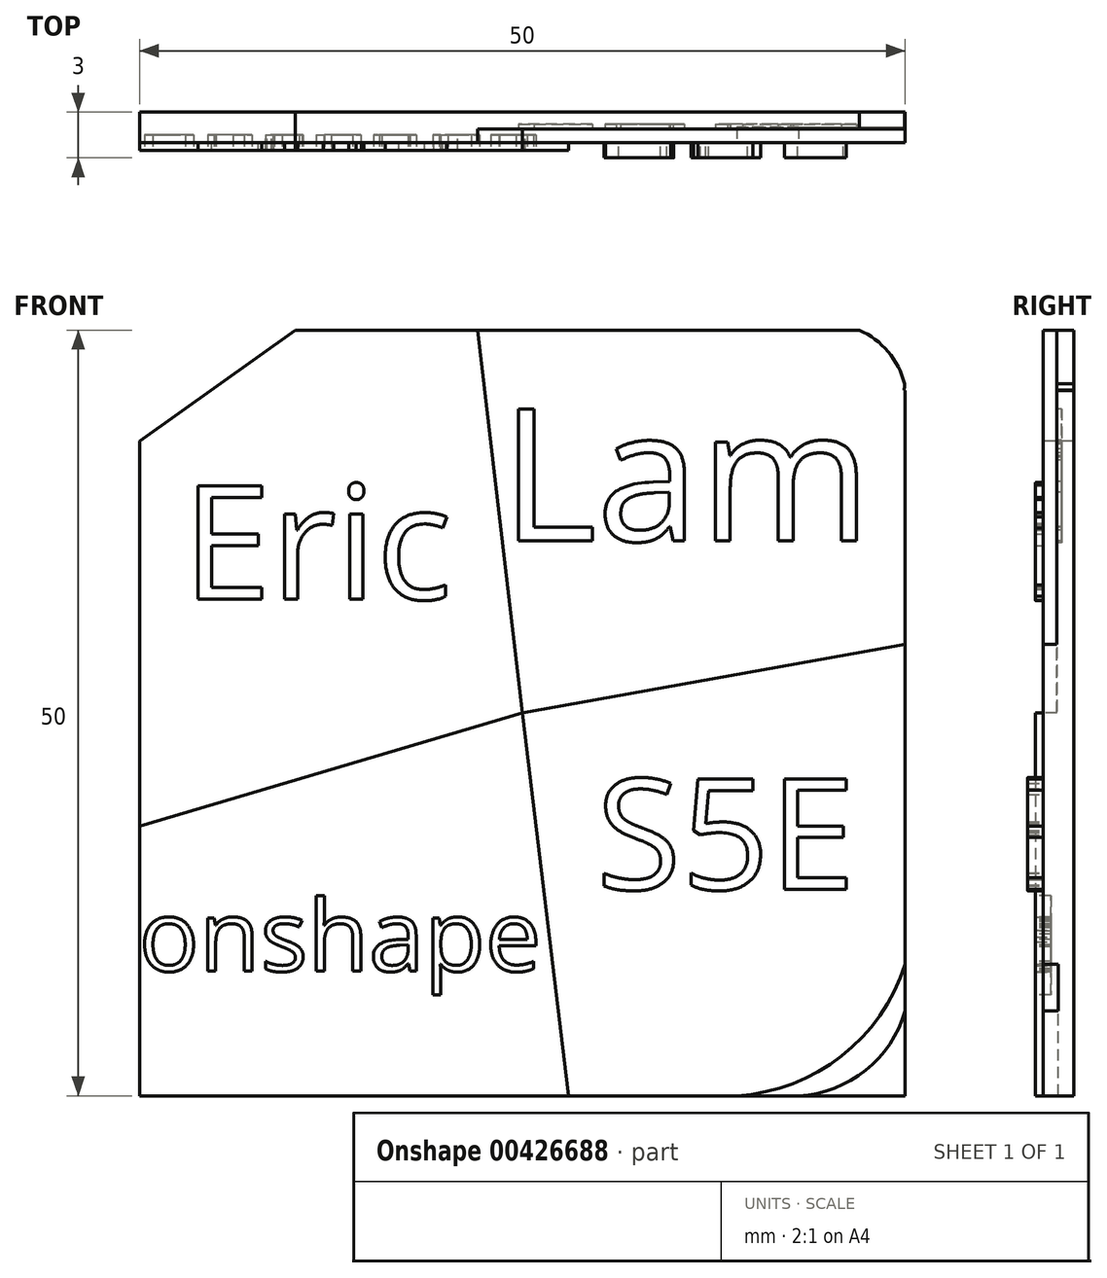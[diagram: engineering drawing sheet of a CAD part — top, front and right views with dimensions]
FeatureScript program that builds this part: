
annotation { "Feature Type Name" : "Feature", "Feature Type Description" : "" }
export const myFeature = defineFeature(function(context is Context, id is Id, definition is map)
    precondition{}
    {
        {
            var Q0;
            Q0=qCreatedBy(makeId("Front.planeOp"),FACE);
            var sketch = newSketch(context, id + "F0", { "sketchPlane" : qUnion([Q0])});
            skLineSegment(sketch, "E0.bottom", {"start": v(25, -25) * mm, "end": v(-25, -25) * mm});
            skLineSegment(sketch, "E0.top", {"start": v(25, 25) * mm, "end": v(-25, 25) * mm});
            skLineSegment(sketch, "E0.left", {"start": v(25, -25) * mm, "end": v(25, 25) * mm});
            skLineSegment(sketch, "E0.right", {"start": v(-25, -25) * mm, "end": v(-25, 25) * mm});
            skPoint(sketch, "E0.middle", {"position": v(0, 0) * mm});
            skLineSegment(sketch, "E1", {"start": v(0, 25) * mm, "end": v(0, 0) * mm});
            skLineSegment(sketch, "E2", {"start": v(0, 0) * mm, "end": v(6.25, -25) * mm});
            skPoint(sketch, "E3.end.orphan", {"position": v(0, -25) * mm});
            skPoint(sketch, "E4.start.orphan", {"position": v(6.25, 0) * mm});
            skPoint(sketch, "E5.end.orphan", {"position": v(12.5, 0) * mm});
            skPoint(sketch, "E6.trimOffspring.end.orphan", {"position": v(25, 0) * mm});
            skLineSegment(sketch, "E7", {"start": v(0, 0) * mm, "end": v(-6.25, -25) * mm});
            skSolve(sketch);
        }
        {
            var Q0;
            Q0 = qSketchRegion(id + "F0", true);
            extrude(context, id + "F1", {"entities" : qUnion([Q0]), "oppositeDirection" : true, "depth" : 2 * mm});
        }
        {
            var Q0;
            Q0=makeQuery(id+"F1.opExtrude","CAP_FACE",FACE,{"disambiguationData":[OSD([sQuery(id+"F0.wireOp",EDGE,"E0.bottom"),sQuery(id+"F0.wireOp",EDGE,"E0.top"),sQuery(id+"F0.wireOp",EDGE,"E0.left"),sQuery(id+"F0.wireOp",EDGE,"E0.right")])],"isStart":true});
            var sketch = newSketch(context, id + "F2", { "sketchPlane" : qUnion([Q0])});
            skLineSegment(sketch, "E8", {"start": v(0, 0) * mm, "end": v(25, 4.5) * mm});
            skPoint(sketch, "E9.orphan", {"position": v(0, 25) * mm});
            skPoint(sketch, "E10.end.orphan", {"position": v(0, -25) * mm});
            skLineSegment(sketch, "E11", {"start": v(0, 0) * mm, "end": v(7.46, -25) * mm});
            skLineSegment(sketch, "E12", {"start": v(-2.93, 25) * mm, "end": v(0, 0) * mm});
            skLineSegment(sketch, "E13", {"start": v(0, 0) * mm, "end": v(-25, -4.25) * mm});
            skSolve(sketch);
        }
        {
            var Q0;
            Q0 = qSketchRegion(id + "F2", true);
            var Q1;
            {var subQ0=sQuery(id+"F2.wireOp",EDGE,"E8");Q1=makeQuery(id+"F2.imprint","IMPRINT",FACE,{"disambiguationData":[TD([[makeQuery(id+"F2.imprint","IMPRINT",EDGE,{"derivedFrom":subQ0}),1.0]])]});}
            extrude(context, id + "F3", {"entities" : qUnion([Q0, Q1]), "operationType" : NewBodyOperationType.REMOVE, "oppositeDirection" : true, "depth" : 0.9 * mm});
        }
        {
            var Q0;
            Q0=makeQuery(id+"F1.opExtrude","CAP_FACE",FACE,{"disambiguationData":[OSD([sQuery(id+"F0.wireOp",EDGE,"E0.bottom"),sQuery(id+"F0.wireOp",EDGE,"E0.top"),sQuery(id+"F0.wireOp",EDGE,"E0.left"),sQuery(id+"F0.wireOp",EDGE,"E0.right")])],"isStart":true});
            var sketch = newSketch(context, id + "F4", { "sketchPlane" : qUnion([Q0])});
            skLineSegment(sketch, "E14", {"start": v(0, 0) * mm, "end": v(-25, -7.38) * mm});
            skLineSegment(sketch, "E15", {"start": v(0, 0) * mm, "end": v(3.03, -25) * mm});
            skSolve(sketch);
        }
        {
            var Q0;
            Q0 = qSketchRegion(id + "F4", true);
            var Q1;
            {var subQ0=sQuery(id+"F4.wireOp",EDGE,"E14");Q1=makeQuery(id+"F4.imprint","IMPRINT",FACE,{"disambiguationData":[TD([[makeQuery(id+"F4.imprint","IMPRINT",EDGE,{"derivedFrom":subQ0}),1.0]])]});}
            extrude(context, id + "F5", {"entities" : qUnion([Q0, Q1]), "operationType" : NewBodyOperationType.ADD, "depth" : 0.5 * mm});
        }
        {
            var Q0;
            {var subQ0=sQuery(id+"F0.wireOp",EDGE,"E0.right");var subQ1=sQuery(id+"F0.wireOp",EDGE,"E0.top");var subQ2=makeQuery(id+"F1.opExtrude","CAP_FACE",FACE,{"disambiguationData":[OSD([sQuery(id+"F0.wireOp",EDGE,"E0.bottom"),subQ1,sQuery(id+"F0.wireOp",EDGE,"E0.left"),subQ0])],"isStart":true});Q0=makeQuery(id+"F5.boolean.opBoolean","SPLIT",FACE,{"disambiguationData":[TD([makeQuery(id+"F1.opExtrude","SWEPT_FACE",FACE,{"disambiguationData":[OSD([subQ1])]})])],"derivedFrom":subQ2});}
            var sketch = newSketch(context, id + "F6", { "sketchPlane" : qUnion([Q0])});
            skText(sketch, "E16", { "text": "Eric\n", "fontName": "OpenSans-Regular.ttf"});
            const initialGuessF6  = {"E16": [-0.02218, 0.00743, 1, 0, 0.00748]};
            skSetInitialGuess(sketch, initialGuessF6);
            skSolve(sketch);
        }
        {
            var Q0;
            Q0 = qSketchRegion(id + "F6", true);
            extrude(context, id + "F7", {"entities" : qUnion([Q0]), "operationType" : NewBodyOperationType.ADD, "depth" : 0.5 * mm});
        }
        {
            var Q0;
            Q0=makeQuery(id+"F3.boolean.opBoolean","COPY",FACE,{"derivedFrom":makeQuery(id+"F3.opExtrude","CAP_FACE",FACE,{"disambiguationData":[OSD([sQuery(id+"F0.wireOp",EDGE,"E0.top"),sQuery(id+"F0.wireOp",EDGE,"E0.left"),sQuery(id+"F2.wireOp",EDGE,"E8"),sQuery(id+"F2.wireOp",EDGE,"E12")])],"isStart":false})});
            var sketch = newSketch(context, id + "F8", { "sketchPlane" : qUnion([Q0])});
            skText(sketch, "E17", { "text": "Lam", "fontName": "OpenSans-Regular.ttf"});
            const initialGuessF8  = {"E17": [-0.00142, 0.01124, 1, 0, 0.00869]};
            skSetInitialGuess(sketch, initialGuessF8);
            skSolve(sketch);
        }
        {
            var Q0;
            Q0 = qSketchRegion(id + "F8", true);
            extrude(context, id + "F9", {"entities" : qUnion([Q0]), "operationType" : NewBodyOperationType.REMOVE, "oppositeDirection" : true, "depth" : 0.3 * mm});
        }
        {
            var Q0;
            Q0=makeQuery(id+"F5.opExtrude","CAP_FACE",FACE,{"disambiguationData":[OSD([sQuery(id+"F0.wireOp",EDGE,"E0.bottom"),sQuery(id+"F0.wireOp",EDGE,"E0.right"),sQuery(id+"F4.wireOp",EDGE,"E14"),sQuery(id+"F4.wireOp",EDGE,"E15")])],"isStart":false});
            var sketch = newSketch(context, id + "F10", { "sketchPlane" : qUnion([Q0])});
            skText(sketch, "E18", { "text": "onshape", "fontName": "OpenSans-Regular.ttf"});
            const initialGuessF10  = {"E18": [-0.02503, -0.01686, 1, 0, 0.00468]};
            skSetInitialGuess(sketch, initialGuessF10);
            skSolve(sketch);
        }
        {
            var Q0;
            Q0 = qSketchRegion(id + "F10", true);
            extrude(context, id + "F11", {"entities" : qUnion([Q0]), "operationType" : NewBodyOperationType.REMOVE, "oppositeDirection" : true, "depth" : 1 * mm});
        }
        {
            var Q0;
            {var subQ0=sQuery(id+"F0.wireOp",EDGE,"E0.left");var subQ1=sQuery(id+"F0.wireOp",EDGE,"E0.bottom");var subQ2=makeQuery(id+"F1.opExtrude","CAP_FACE",FACE,{"disambiguationData":[OSD([subQ1,sQuery(id+"F0.wireOp",EDGE,"E0.top"),subQ0,sQuery(id+"F0.wireOp",EDGE,"E0.right")])],"isStart":true});Q0=makeQuery(id+"F5.boolean.opBoolean","SPLIT",FACE,{"disambiguationData":[TD([makeQuery(id+"F1.opExtrude","SWEPT_FACE",FACE,{"disambiguationData":[OSD([subQ1])]})])],"derivedFrom":subQ2});}
            var sketch = newSketch(context, id + "F12", { "sketchPlane" : qUnion([Q0])});
            skText(sketch, "E19", { "text": "S5E", "fontName": "OpenSans-Regular.ttf"});
            const initialGuessF12  = {"E19": [0.00482, -0.01152, 1, 0, 0.00727]};
            skSetInitialGuess(sketch, initialGuessF12);
            skSolve(sketch);
        }
        {
            var Q0;
            Q0 = qSketchRegion(id + "F12", true);
            extrude(context, id + "F13", {"entities" : qUnion([Q0]), "operationType" : NewBodyOperationType.ADD, "depth" : 1 * mm});
        }
        {
            var Q0;
            {var subQ0=sQuery(id+"F0.wireOp",EDGE,"E0.right");var subQ1=sQuery(id+"F0.wireOp",EDGE,"E0.top");var subQ2=makeQuery(id+"F1.opExtrude","CAP_FACE",FACE,{"disambiguationData":[OSD([sQuery(id+"F0.wireOp",EDGE,"E0.bottom"),subQ1,sQuery(id+"F0.wireOp",EDGE,"E0.left"),subQ0])],"isStart":true});Q0=makeQuery(id+"F5.boolean.opBoolean","SPLIT",FACE,{"disambiguationData":[TD([makeQuery(id+"F1.opExtrude","SWEPT_FACE",FACE,{"disambiguationData":[OSD([subQ1])]})])],"derivedFrom":subQ2});}
            var sketch = newSketch(context, id + "F14", { "sketchPlane" : qUnion([Q0])});
            skLineSegment(sketch, "E20", {"start": v(-25, 17.75) * mm, "end": v(-14.82, 25) * mm});
            skLineSegment(sketch, "E21", {"start": v(17.85, 25) * mm, "end": v(25.21, 19.55) * mm});
            skPoint(sketch, "E21.startSnap0", {"position": v(-13.96, 25) * mm});
            skSolve(sketch);
        }
        {
            var Q0;
            Q0 = qSketchRegion(id + "F14", true);
            var Q1;
            {var subQ0=sQuery(id+"F14.wireOp",EDGE,"E20");Q1=makeQuery(id+"F14.imprint","IMPRINT",FACE,{"disambiguationData":[TD([[makeQuery(id+"F14.imprint","IMPRINT",EDGE,{"derivedFrom":subQ0}),1.0]])]});}
            extrude(context, id + "F15", {"entities" : qUnion([Q0, Q1]), "operationType" : NewBodyOperationType.REMOVE, "oppositeDirection" : true, "depth" : 25 * mm});
        }
        {
            var Q0;
            {var subQ0=sQuery(id+"F0.wireOp",EDGE,"E0.left");var subQ1=sQuery(id+"F0.wireOp",EDGE,"E0.top");var subQ2=sQuery(id+"F2.wireOp",EDGE,"E8");var subQ3=sQuery(id+"F2.wireOp",EDGE,"E12");Q0=makeQuery(id+"F9.boolean.opBoolean","SPLIT",FACE,{"disambiguationData":[TD([makeQuery(id+"F1.opExtrude","SWEPT_FACE",FACE,{"disambiguationData":[OSD([subQ1])]})])],"derivedFrom":makeQuery(id+"F3.boolean.opBoolean","COPY",FACE,{"derivedFrom":makeQuery(id+"F3.opExtrude","CAP_FACE",FACE,{"disambiguationData":[OSD([subQ1,subQ0,subQ2,subQ3])],"isStart":false})})});}
            var sketch = newSketch(context, id + "F16", { "sketchPlane" : qUnion([Q0])});
            skPoint(sketch, "E22.center.orphan", {"position": v(22.02, 23.03) * mm});
            skArc(sketch, "E23", {"start": v(24.93, 21.1) * mm, "mid": v(24.95, 21.3) * mm, "end": v(24.96, 21.5) * mm});
            skArc(sketch, "E24", {"start": v(24.96, 21.5) * mm, "mid": v(22.02, 25) * mm, "end": v(17.46, 24.8) * mm});
            skLineSegment(sketch, "E25.trimOffspring", {"start": v(24.93, 21.1) * mm, "end": v(25, 21.06) * mm});
            skPoint(sketch, "E26.start.orphan", {"position": v(19.04, 25) * mm});
            skSolve(sketch);
        }
        {
            var Q0;
            Q0 = qSketchRegion(id + "F16", true);
            var Q1;
            {var subQ6=sQuery(id+"F16.wireOp",EDGE,"E23");Q1=makeQuery(id+"F16.imprint","IMPRINT",FACE,{"disambiguationData":[TD([[makeQuery(id+"F16.imprint","IMPRINT",EDGE,{"derivedFrom":subQ6}),-1.0]])]});}
            extrude(context, id + "F17", {"entities" : qUnion([Q0, Q1]), "operationType" : NewBodyOperationType.REMOVE, "oppositeDirection" : true, "depth" : 25 * mm});
        }
        {
            var Q0;
            {var subQ0=sQuery(id+"F0.wireOp",EDGE,"E0.left");var subQ1=sQuery(id+"F0.wireOp",EDGE,"E0.bottom");var subQ2=makeQuery(id+"F1.opExtrude","CAP_FACE",FACE,{"disambiguationData":[OSD([subQ1,sQuery(id+"F0.wireOp",EDGE,"E0.top"),subQ0,sQuery(id+"F0.wireOp",EDGE,"E0.right")])],"isStart":true});Q0=makeQuery(id+"F5.boolean.opBoolean","SPLIT",FACE,{"disambiguationData":[TD([makeQuery(id+"F1.opExtrude","SWEPT_FACE",FACE,{"disambiguationData":[OSD([subQ1])]})])],"derivedFrom":subQ2});}
            var sketch = newSketch(context, id + "F18", { "sketchPlane" : qUnion([Q0])});
            skArc(sketch, "E27", {"start": v(17.2, -25) * mm, "mid": v(22.07, -23.6) * mm, "end": v(25, -19.45) * mm});
            skArc(sketch, "E28", {"start": v(14.02, -25) * mm, "mid": v(20.84, -22.41) * mm, "end": v(25, -16.41) * mm});
            skSolve(sketch);
        }
        {
            var Q0;
            Q0 = qSketchRegion(id + "F18", true);
            var Q1;
            {var subQ3=sQuery(id+"F18.wireOp",EDGE,"E28");Q1=makeQuery(id+"F18.imprint","IMPRINT",FACE,{"disambiguationData":[TD([[makeQuery(id+"F18.imprint","IMPRINT",EDGE,{"derivedFrom":subQ3}),-1.0]])]});}
            extrude(context, id + "F19", {"entities" : qUnion([Q0, Q1]), "operationType" : NewBodyOperationType.REMOVE, "oppositeDirection" : true, "depth" : 1 * mm});
        }
    });
